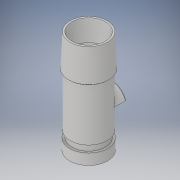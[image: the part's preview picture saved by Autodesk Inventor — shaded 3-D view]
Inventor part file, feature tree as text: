
AUTODESK INVENTOR PART (.ipt)
format: ipt  version: 2019.1 (Build 231200000, 200)  size: 410,112 bytes
history: native  units: mm
features: extrude x7, sketch x7, chamfer x2, other x1, fillet x1, plane x1, draft x1
ambient origin geometry x8: Origin, YZ Plane, XZ Plane, XY Plane, X Axis, Y Axis, Z Axis, Center Point
bodies: Solid1 (feature_tree)
feature tree (20):
  other  "CrossSection1"
  extrude  "Extrusion1"  Depth=35.0mm
  extrude  "Extrusion2"  Depth=10.0mm
  extrude  "Extrusion3"  Depth=50.0mm TaperAngle=0.0deg
  fillet  "Fillet1"  Radius=1.0mm
  plane  "Work Plane1"
  extrude  "Extrusion4"  Depth=10.0mm
  chamfer  "Chamfer1"  Distance=2.0mm
  extrude  "Extrusion5"  Depth=30.0mm
  extrude  "Extrusion6"  Depth=30.0mm
  chamfer  "Chamfer3"  Distance=10.0mm
  extrude  "Extrusion7"  Depth=30.0mm TaperAngle=0.0deg
  draft  "FaceDraft4"
  sketch  "Sketch1"  dims[d0=29.5mm d1=35.0mm]
  sketch  "Sketch2"  dims[d2=10.0mm d3=0.0mm d4=31.0mm]
  sketch  "Sketch3"  dims[d5=5.0mm d6=0.0mm d7=50.0mm d8=0.0mm d9=1.0mm]
  sketch  "Sketch4"  dims[d10=37.0mm d16=10.0mm]
  sketch  "Sketch5"  dims[d17=12.5mm]
  sketch  "Sketch6"  dims[d18=12.5mm]
  sketch  "Sketch9"  dims[d19=5.0mm d20=2.0mm d21=2.0mm d22=44.048322mm d23=10.0mm d24=0.0mm d25=4.0mm d26=0.0mm d27=1.5mm d28=2.0mm d29=45.0deg d30=1.5mm d31=0.0mm d32=37.0mm d33=30.0mm d34=0.0mm d38=0.5mm d39=2.0mm d40=45.0deg d44=0.5mm d45=2.0mm d46=-2.25mm d47=20.0mm d51=0.0mm d52=0.0mm d56=0.436332mm]
